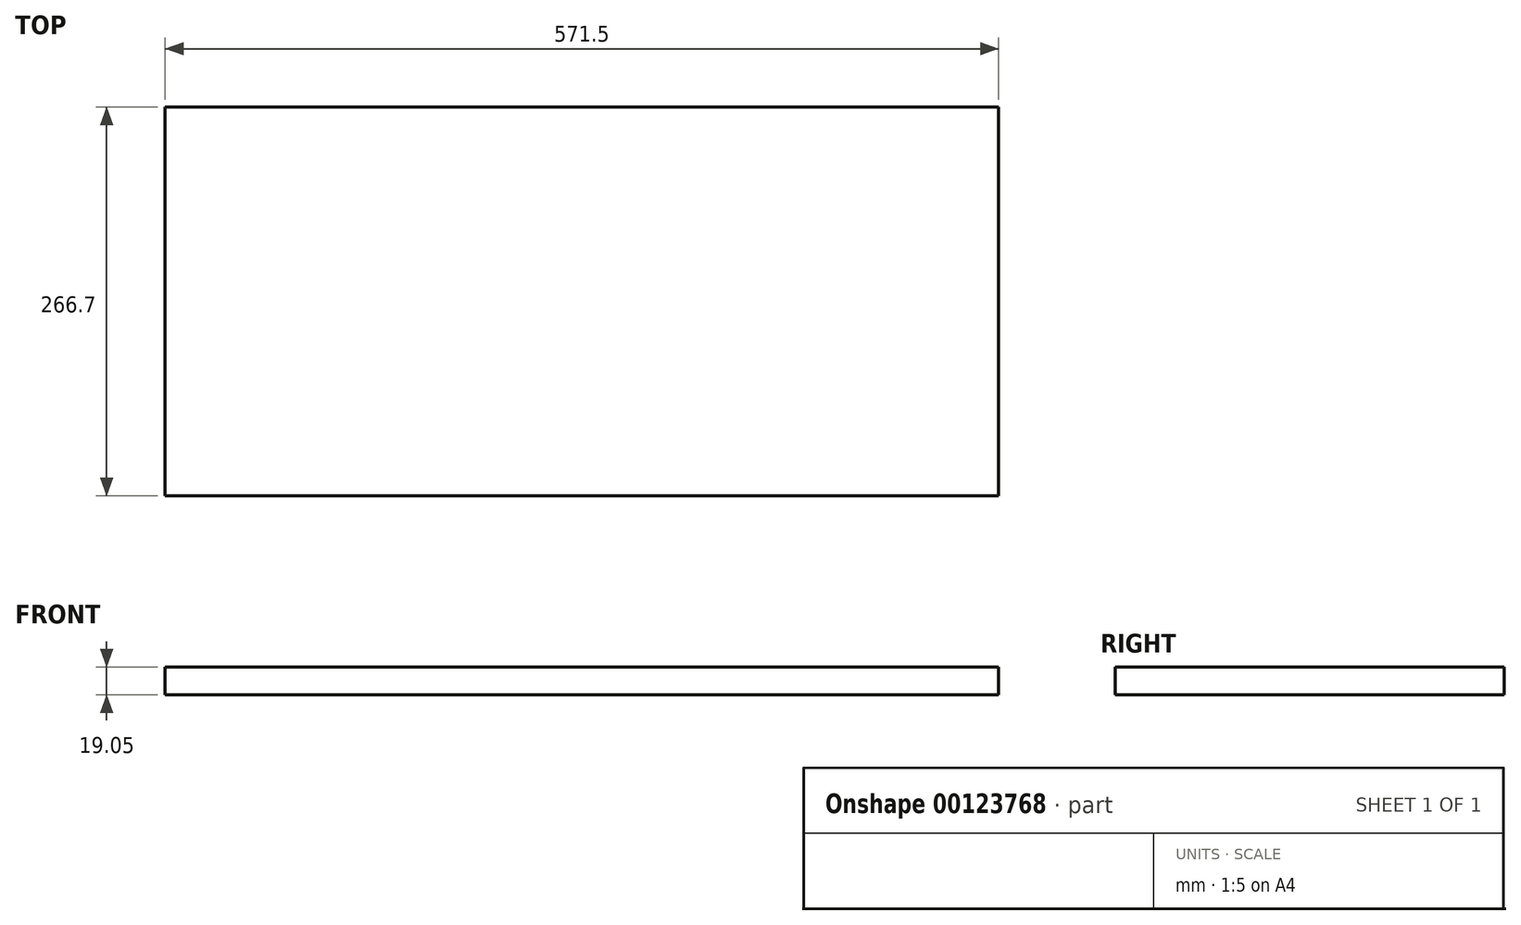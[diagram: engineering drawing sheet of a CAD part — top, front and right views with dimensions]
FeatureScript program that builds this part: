
annotation { "Feature Type Name" : "Feature", "Feature Type Description" : "" }
export const myFeature = defineFeature(function(context is Context, id is Id, definition is map)
    precondition{}
    {
        {
            var Q0;
            Q0=qCreatedBy(makeId("Top.planeOp"),FACE);
            var sketch = newSketch(context, id + "F0", { "sketchPlane" : qUnion([Q0])});
            skLineSegment(sketch, "E0.bottom", {"start": v(-186.26, -113.45) * mm, "end": v(385.24, -113.45) * mm});
            skLineSegment(sketch, "E0.top", {"start": v(-186.26, 153.25) * mm, "end": v(385.24, 153.25) * mm});
            skLineSegment(sketch, "E0.left", {"start": v(-186.26, -113.45) * mm, "end": v(-186.26, 153.25) * mm});
            skLineSegment(sketch, "E0.right", {"start": v(385.24, -113.45) * mm, "end": v(385.24, 153.25) * mm});
            skSolve(sketch);
        }
        {
            var Q0;
            Q0=makeQuery(id+"F0.imprint","IMPRINT",FACE,{"disambiguationData":[TD([[makeQuery(id+"F0.imprint","IMPRINT",EDGE,{"derivedFrom":sQuery(id+"F0.wireOp",EDGE,"E0.bottom")}),1.0]])]});
            extrude(context, id + "F1", {"entities" : qUnion([Q0]), "depth" : 19.05 * mm});
        }
    });
